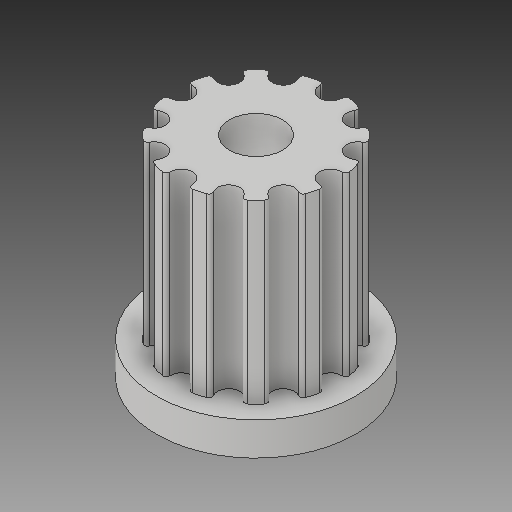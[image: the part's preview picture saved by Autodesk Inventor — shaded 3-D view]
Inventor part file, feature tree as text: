
AUTODESK INVENTOR PART (.ipt)
format: ipt  version: 2018.2 (Build 222227000, 227)  size: 195,072 bytes
history: native  units: mm
features: extrude x3, sketch x3, pattern_circular x1
ambient origin geometry x8: Origin, YZ Plane, XZ Plane, XY Plane, X Axis, Y Axis, Z Axis, Center Point
bodies: Solid1 (feature_tree)
feature tree (7):
  extrude  "Extrusion1"  Depth=0.5mm
  extrude  "Extrusion2"  Depth=0.15mm TaperAngle=0.0deg
  pattern_circular  "Circular Pattern1"  [2 undecoded]
  extrude  "Extrusion3"  TaperAngle=0.0deg  [1 undecoded]
  sketch  "Sketch1"  dims[d8=0.0mm d9=0.5mm]
  sketch  "Sketch2"  dims[d10=0.15mm d12=7.0mm d13=0.0mm]
  sketch  "Sketch3"  dims[d15=360.0deg d18=2.4mm d20=0.0mm]
note: 3 required parameter values undecoded (feature->parameter linkage not recoverable at this tier; creation-order binding heuristic only, values carry confidence <= 0.55)
